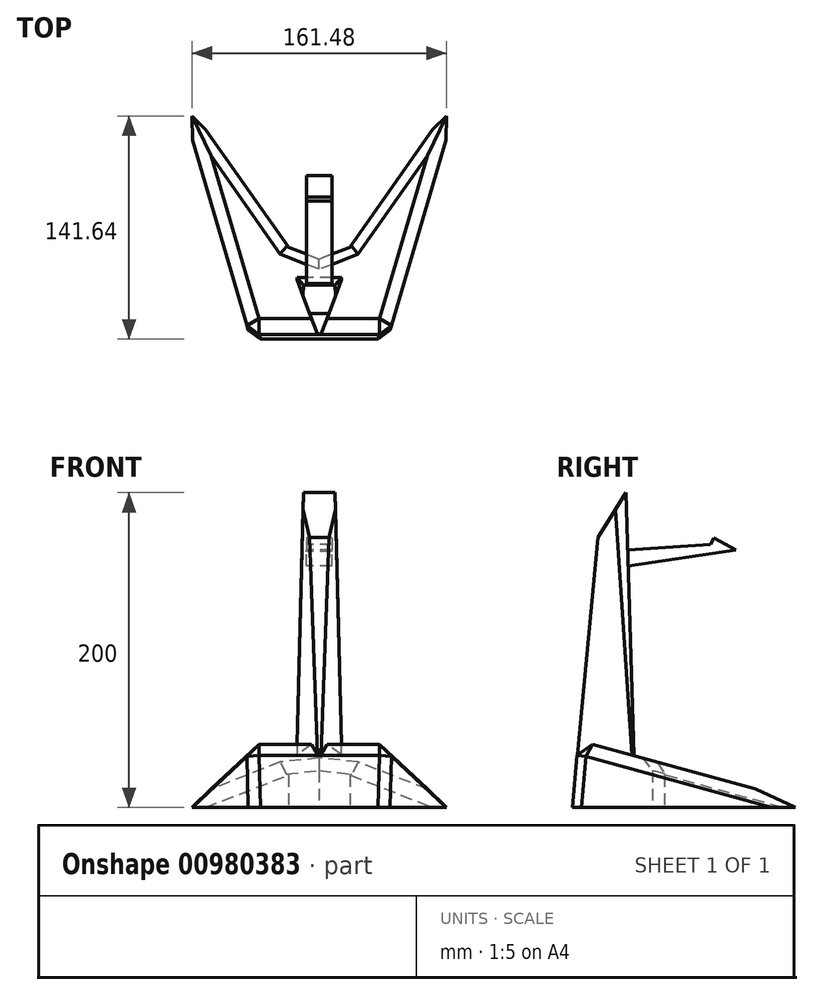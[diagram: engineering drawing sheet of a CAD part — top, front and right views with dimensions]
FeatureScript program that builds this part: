
annotation { "Feature Type Name" : "Feature", "Feature Type Description" : "" }
export const myFeature = defineFeature(function(context is Context, id is Id, definition is map)
    precondition{}
    {
        {
            var Q0;
            Q0=qCreatedBy(makeId("Right.planeOp"),FACE);
            var sketch = newSketch(context, id + "F0", { "sketchPlane" : qUnion([Q0])});
            skLineSegment(sketch, "E0", {"start": v(0, -53.85) * mm, "end": v(0, 145.78) * mm, "construction": true});
            skLineSegment(sketch, "E1", {"start": v(8.95, 145.78) * mm, "end": v(-9.05, 117.3) * mm});
            skLineSegment(sketch, "E2", {"start": v(-9.05, 117.3) * mm, "end": v(-25.25, -54.22) * mm});
            skLineSegment(sketch, "E3", {"start": v(-25.25, -54.22) * mm, "end": v(14.75, -54.22) * mm});
            skLineSegment(sketch, "E4", {"start": v(14.75, -54.22) * mm, "end": v(8.95, 145.78) * mm});
            skLineSegment(sketch, "E5", {"start": v(21.3, 145.78) * mm, "end": v(-67.15, 145.78) * mm, "construction": true});
            skSolve(sketch);
        }
        {
            var Q0;
            Q0 = qSketchRegion(id + "F0", true);
            extrude(context, id + "F1", {"entities" : qUnion([Q0]), "depth" : 30 * mm, "offsetDistance" : 25 * mm, "symmetric" : true});
        }
        {
            var Q0;
            Q0=makeQuery(id+"F1.opExtrude","SWEPT_FACE",FACE,{"disambiguationData":[OSD([sQuery(id+"F0.wireOp",EDGE,"E4")])]});
            var sketch = newSketch(context, id + "F2", { "sketchPlane" : qUnion([Q0])});
            skLineSegment(sketch, "E6", {"start": v(-15, -54.62) * mm, "end": v(-10, 145.46) * mm});
            skLineSegment(sketch, "E7", {"start": v(-10, 145.46) * mm, "end": v(10, 145.46) * mm});
            skLineSegment(sketch, "E8", {"start": v(10, 145.46) * mm, "end": v(15, -54.62) * mm});
            skSolve(sketch);
        }
        {
            var Q0;
            {var subQ0=sQuery(id+"F2.wireOp",EDGE,"E6");Q0=makeQuery(id+"F2.imprint","IMPRINT",FACE,{"disambiguationData":[TD([[makeQuery(id+"F2.imprint","IMPRINT",EDGE,{"derivedFrom":subQ0}),1.0]])]});}
            var Q1;
            {var subQ0=sQuery(id+"F2.wireOp",EDGE,"E8");Q1=makeQuery(id+"F2.imprint","IMPRINT",FACE,{"disambiguationData":[TD([[makeQuery(id+"F2.imprint","IMPRINT",EDGE,{"derivedFrom":subQ0}),1.0]])]});}
            extrude(context, id + "F3", {"entities" : qUnion([Q0, Q1]), "operationType" : NewBodyOperationType.REMOVE, "endBound" : BoundingType.THROUGH_ALL, "oppositeDirection" : true, "depth" : 142.4 * mm, "offsetDistance" : 25 * mm});
        }
        {
            var Q0;
            Q0=makeQuery(id+"F1.opExtrude","SWEPT_FACE",FACE,{"disambiguationData":[OSD([sQuery(id+"F0.wireOp",EDGE,"E3")])]});
            var sketch = newSketch(context, id + "F4", { "sketchPlane" : qUnion([Q0])});
            skLineSegment(sketch, "E9", {"start": v(15, -14.75) * mm, "end": v(0, 25.25) * mm});
            skLineSegment(sketch, "E10", {"start": v(0, 25.25) * mm, "end": v(-15, -14.75) * mm});
            skLineSegment(sketch, "E11", {"start": v(-15, -14.75) * mm, "end": v(15, -14.75) * mm});
            skSolve(sketch);
        }
        {
            var Q0;
            {var subQ0=sQuery(id+"F4.wireOp",EDGE,"E9");Q0=makeQuery(id+"F4.imprint","IMPRINT",FACE,{"disambiguationData":[TD([[makeQuery(id+"F4.imprint","IMPRINT",EDGE,{"derivedFrom":subQ0}),-1.0]])]});}
            var Q1;
            {var subQ0=sQuery(id+"F4.wireOp",EDGE,"E10");Q1=makeQuery(id+"F4.imprint","IMPRINT",FACE,{"disambiguationData":[TD([[makeQuery(id+"F4.imprint","IMPRINT",EDGE,{"derivedFrom":subQ0}),-1.0]])]});}
            extrude(context, id + "F5", {"entities" : qUnion([Q0, Q1]), "operationType" : NewBodyOperationType.REMOVE, "endBound" : BoundingType.THROUGH_ALL, "oppositeDirection" : true, "depth" : 25 * mm, "offsetDistance" : 25 * mm});
        }
        {
            var Q0;
            Q0=qCreatedBy(makeId("Right.planeOp"),FACE);
            var sketch = newSketch(context, id + "F6", { "sketchPlane" : qUnion([Q0])});
            skLineSegment(sketch, "E12", {"start": v(-32.9, -54.22) * mm, "end": v(72.95, -54.22) * mm, "construction": true});
            skLineSegment(sketch, "E13", {"start": v(-25.25, -69.8) * mm, "end": v(-25.25, 21.5) * mm, "construction": true});
            skLineSegment(sketch, "E14", {"start": v(-21.57, -11.58) * mm, "end": v(133.5, -54.22) * mm});
            skLineSegment(sketch, "E15", {"start": v(133.5, -54.22) * mm, "end": v(-25.25, -54.22) * mm});
            skLineSegment(sketch, "E16", {"start": v(-25.25, -54.22) * mm, "end": v(-21.57, -11.58) * mm});
            skSolve(sketch);
        }
        {
            var Q0;
            Q0=makeQuery(id+"F6.imprint","IMPRINT",FACE,{"disambiguationData":[TD([[makeQuery(id+"F6.imprint","IMPRINT",EDGE,{"derivedFrom":sQuery(id+"F6.wireOp",EDGE,"E14")}),-1.0]])]});
            extrude(context, id + "F7", {"entities" : qUnion([Q0]), "operationType" : NewBodyOperationType.ADD, "depth" : 180 * mm, "offsetDistance" : 25 * mm, "symmetric" : true});
        }
        {
            var Q0;
            Q0=makeQuery(id+"F7.boolean.opBoolean","MERGE",FACE,{"derivedFrom":[makeQuery(id+"F1.opExtrude","SWEPT_FACE",FACE,{"disambiguationData":[OSD([sQuery(id+"F0.wireOp",EDGE,"E3")])]}),makeQuery(id+"F7.opExtrude","SWEPT_FACE",FACE,{"disambiguationData":[OSD([sQuery(id+"F6.wireOp",EDGE,"E15")])]})]});
            var sketch = newSketch(context, id + "F8", { "sketchPlane" : qUnion([Q0])});
            skLineSegment(sketch, "E17", {"start": v(-43.36, 25.25) * mm, "end": v(-90, -133.5) * mm});
            skLineSegment(sketch, "E18", {"start": v(-19.62, -33.13) * mm, "end": v(-90, -133.5) * mm});
            skLineSegment(sketch, "E19", {"start": v(-43.36, 25.25) * mm, "end": v(0, 25.25) * mm});
            skLineSegment(sketch, "E20", {"start": v(-19.62, -33.13) * mm, "end": v(0, -25.63) * mm});
            skLineSegment(sketch, "E21", {"start": v(0, 65.34) * mm, "end": v(0, -125.6) * mm, "construction": true});
            skLineSegment(sketch, "E22.MirrorCS", {"start": v(43.36, 25.25) * mm, "end": v(0, 25.25) * mm});
            skLineSegment(sketch, "E23.MirrorCS", {"start": v(43.36, 25.25) * mm, "end": v(90, -133.5) * mm});
            skLineSegment(sketch, "E24.MirrorCS", {"start": v(19.62, -33.13) * mm, "end": v(90, -133.5) * mm});
            skLineSegment(sketch, "E25.MirrorCS", {"start": v(19.62, -33.13) * mm, "end": v(0, -25.63) * mm});
            skSolve(sketch);
        }
        {
            var Q0;
            {var subQ0=sQuery(id+"F8.wireOp",EDGE,"E17");Q0=makeQuery(id+"F8.imprint","IMPRINT",FACE,{"disambiguationData":[TD([[makeQuery(id+"F8.imprint","IMPRINT",EDGE,{"derivedFrom":subQ0}),-1.0]])]});}
            var Q1;
            {var subQ0=sQuery(id+"F8.wireOp",EDGE,"E23.MirrorCS");Q1=makeQuery(id+"F8.imprint","IMPRINT",FACE,{"disambiguationData":[TD([[makeQuery(id+"F8.imprint","IMPRINT",EDGE,{"derivedFrom":subQ0}),1.0]])]});}
            var Q2;
            Q2=makeQuery(id+"F8.imprint","IMPRINT",FACE,{"disambiguationData":[TD([[makeQuery(id+"F8.imprint","IMPRINT",EDGE,{"derivedFrom":sQuery(id+"F8.wireOp",EDGE,"E18")}),1.0]])]});
            extrude(context, id + "F9", {"entities" : qUnion([Q0, Q1, Q2]), "operationType" : NewBodyOperationType.REMOVE, "oppositeDirection" : true, "depth" : 73.5 * mm, "offsetDistance" : 25 * mm});
        }
        {
            var Q0;
            Q0=makeQuery(id+"F9.boolean.opBoolean","INTERSECT",EDGE,{"derivedFrom":[makeQuery(id+"F7.opExtrude","SWEPT_FACE",FACE,{"disambiguationData":[OSD([sQuery(id+"F6.wireOp",EDGE,"E14")])]}),makeQuery(id+"F9.opExtrude","SWEPT_FACE",FACE,{"disambiguationData":[OSD([sQuery(id+"F8.wireOp",EDGE,"E17")])]})]});
            var Q1;
            Q1=makeQuery(id+"F9.boolean.opBoolean","INTERSECT",EDGE,{"derivedFrom":[makeQuery(id+"F7.opExtrude","SWEPT_FACE",FACE,{"disambiguationData":[OSD([sQuery(id+"F6.wireOp",EDGE,"E14")])]}),makeQuery(id+"F9.opExtrude","SWEPT_FACE",FACE,{"disambiguationData":[OSD([sQuery(id+"F8.wireOp",EDGE,"E23.MirrorCS")])]})]});
            var Q2;
            Q2=makeQuery(id+"F7.opExtrude","SWEPT_EDGE",EDGE,{"disambiguationData":[OSD([sQuery(id+"F6.wireOp",EDGE,"E14"),sQuery(id+"F6.wireOp",EDGE,"E16")])]});
            var Q3;
            Q3=makeQuery(id+"F9.boolean.opBoolean","INTERSECT",EDGE,{"derivedFrom":[makeQuery(id+"F7.opExtrude","SWEPT_FACE",FACE,{"disambiguationData":[OSD([sQuery(id+"F6.wireOp",EDGE,"E14")])]}),makeQuery(id+"F9.opExtrude","SWEPT_FACE",FACE,{"disambiguationData":[OSD([sQuery(id+"F8.wireOp",EDGE,"E25.MirrorCS")])]})]});
            var Q4;
            Q4=makeQuery(id+"F9.boolean.opBoolean","INTERSECT",EDGE,{"derivedFrom":[makeQuery(id+"F7.opExtrude","SWEPT_FACE",FACE,{"disambiguationData":[OSD([sQuery(id+"F6.wireOp",EDGE,"E14")])]}),makeQuery(id+"F9.opExtrude","SWEPT_FACE",FACE,{"disambiguationData":[OSD([sQuery(id+"F8.wireOp",EDGE,"E20")])]})]});
            var Q5;
            Q5=makeQuery(id+"F9.boolean.opBoolean","INTERSECT",EDGE,{"derivedFrom":[makeQuery(id+"F7.opExtrude","SWEPT_FACE",FACE,{"disambiguationData":[OSD([sQuery(id+"F6.wireOp",EDGE,"E14")])]}),makeQuery(id+"F9.opExtrude","SWEPT_FACE",FACE,{"disambiguationData":[OSD([sQuery(id+"F8.wireOp",EDGE,"E18")])]})]});
            var Q6;
            Q6=makeQuery(id+"F9.boolean.opBoolean","INTERSECT",EDGE,{"derivedFrom":[makeQuery(id+"F7.opExtrude","SWEPT_FACE",FACE,{"disambiguationData":[OSD([sQuery(id+"F6.wireOp",EDGE,"E14")])]}),makeQuery(id+"F9.opExtrude","SWEPT_FACE",FACE,{"disambiguationData":[OSD([sQuery(id+"F8.wireOp",EDGE,"E24.MirrorCS")])]})]});
            var Q7;
            Q7=makeQuery(id+"F9.boolean.opBoolean","INTERSECT",EDGE,{"derivedFrom":[makeQuery(id+"F7.opExtrude","SWEPT_FACE",FACE,{"disambiguationData":[OSD([sQuery(id+"F6.wireOp",EDGE,"E16")])]}),makeQuery(id+"F9.opExtrude","SWEPT_FACE",FACE,{"disambiguationData":[OSD([sQuery(id+"F8.wireOp",EDGE,"E17")])]})]});
            var Q8;
            Q8=makeQuery(id+"F9.boolean.opBoolean","INTERSECT",EDGE,{"derivedFrom":[makeQuery(id+"F7.opExtrude","SWEPT_FACE",FACE,{"disambiguationData":[OSD([sQuery(id+"F6.wireOp",EDGE,"E16")])]}),makeQuery(id+"F9.opExtrude","SWEPT_FACE",FACE,{"disambiguationData":[OSD([sQuery(id+"F8.wireOp",EDGE,"E23.MirrorCS")])]})]});
            chamfer(context, id + "F10", {"entities" : qUnion([Q0, Q1, Q2, Q3, Q4, Q5, Q6, Q7, Q8]), "width" : 8 * mm, "tangentPropagation" : true});
        }
        {
            var Q0;
            Q0=qCreatedBy(makeId("Right.planeOp"),FACE);
            var sketch = newSketch(context, id + "F11", { "sketchPlane" : qUnion([Q0])});
            skLineSegment(sketch, "E26", {"start": v(-9.05, 145.6) * mm, "end": v(-9.05, 55.9) * mm, "construction": true});
            skLineSegment(sketch, "E27", {"start": v(9.8, 99.03) * mm, "end": v(78.6, 109.35) * mm});
            skLineSegment(sketch, "E28", {"start": v(64.84, 117.03) * mm, "end": v(78.6, 109.35) * mm});
            skLineSegment(sketch, "E29", {"start": v(64.84, 117.03) * mm, "end": v(62.45, 112.74) * mm});
            skLineSegment(sketch, "E30", {"start": v(62.45, 112.74) * mm, "end": v(10.07, 109.35) * mm});
            skLineSegment(sketch, "E31", {"start": v(9.8, 99.03) * mm, "end": v(10.07, 109.35) * mm});
            skSolve(sketch);
        }
        {
            var Q0;
            Q0=makeQuery(id+"F11.imprint","IMPRINT",FACE,{"disambiguationData":[TD([[makeQuery(id+"F11.imprint","IMPRINT",EDGE,{"derivedFrom":sQuery(id+"F11.wireOp",EDGE,"E27")}),1.0]])]});
            extrude(context, id + "F12", {"entities" : qUnion([Q0]), "operationType" : NewBodyOperationType.ADD, "depth" : 16 * mm, "offsetDistance" : 25 * mm, "symmetric" : true});
        }
    });
